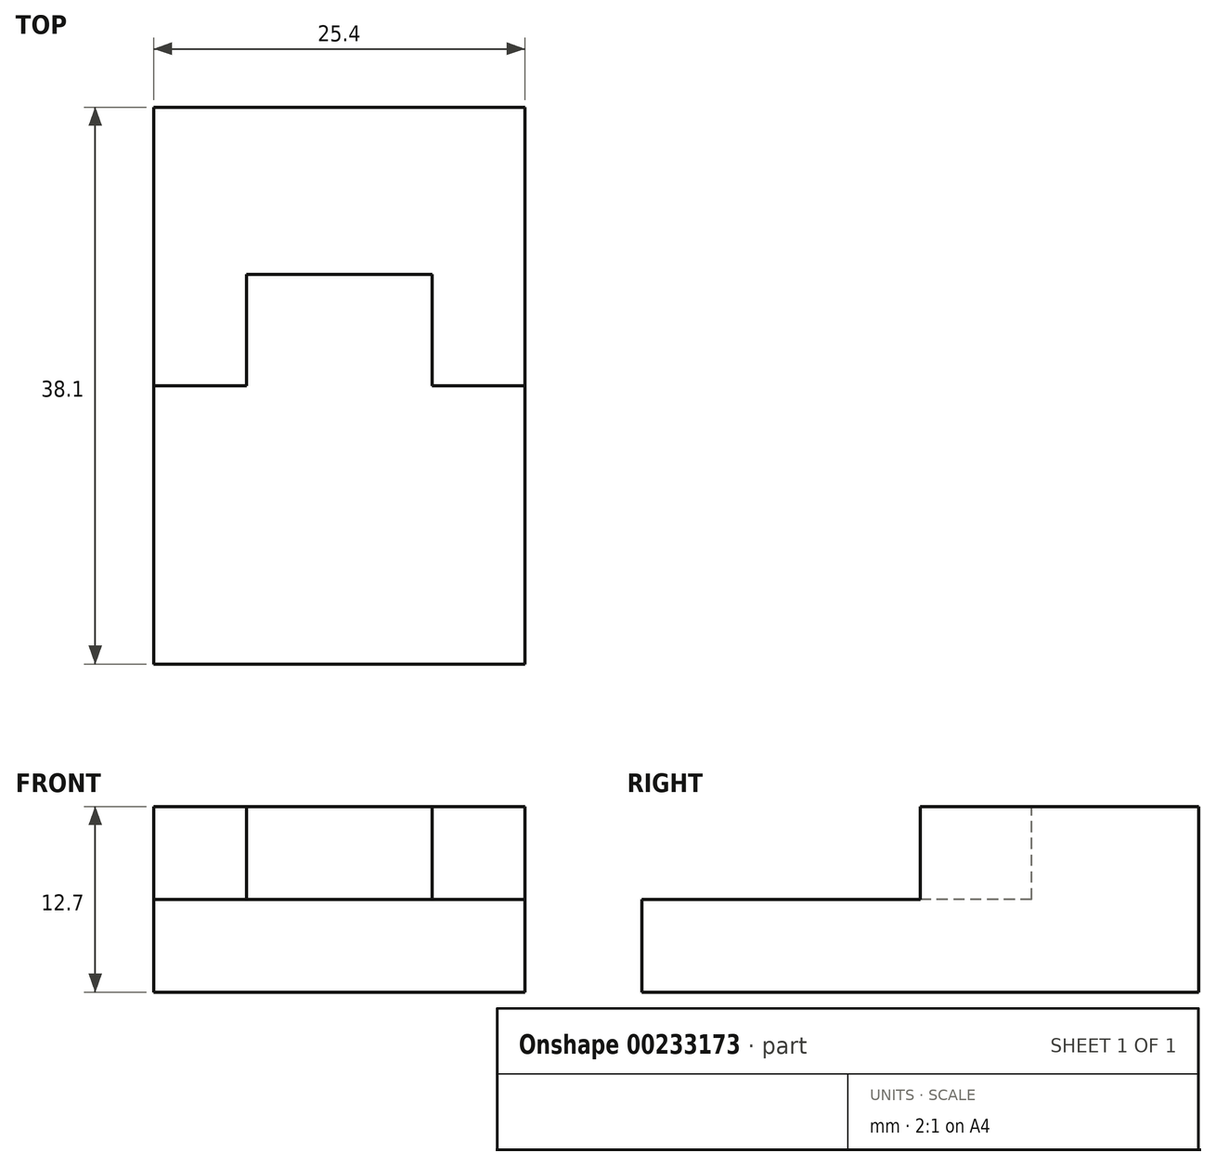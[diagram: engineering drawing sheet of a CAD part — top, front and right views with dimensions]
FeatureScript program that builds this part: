
annotation { "Feature Type Name" : "Feature", "Feature Type Description" : "" }
export const myFeature = defineFeature(function(context is Context, id is Id, definition is map)
    precondition{}
    {
        {
            var Q0;
            Q0=qCreatedBy(makeId("Top.planeOp"),FACE);
            var sketch = newSketch(context, id + "F0", { "sketchPlane" : qUnion([Q0])});
            skLineSegment(sketch, "E0.bottom", {"start": v(12.7, 19.05) * mm, "end": v(-12.7, 19.05) * mm});
            skLineSegment(sketch, "E0.top", {"start": v(12.7, -19.05) * mm, "end": v(-12.7, -19.05) * mm});
            skLineSegment(sketch, "E0.left", {"start": v(12.7, 19.05) * mm, "end": v(12.7, -19.05) * mm});
            skLineSegment(sketch, "E0.right", {"start": v(-12.7, 19.05) * mm, "end": v(-12.7, -19.05) * mm});
            skPoint(sketch, "E0.middle", {"position": v(0, 0) * mm});
            skSolve(sketch);
        }
        {
            var Q0;
            Q0 = qSketchRegion(id + "F0", true);
            extrude(context, id + "F1", {"entities" : qUnion([Q0]), "depth" : 6.35 * mm});
        }
        {
            var Q0;
            Q0=makeQuery(id+"F1.opExtrude","CAP_FACE",FACE,{"disambiguationData":[OSD([sQuery(id+"F0.wireOp",EDGE,"E0.bottom"),sQuery(id+"F0.wireOp",EDGE,"E0.top"),sQuery(id+"F0.wireOp",EDGE,"E0.left"),sQuery(id+"F0.wireOp",EDGE,"E0.right")])],"isStart":false});
            var sketch = newSketch(context, id + "F2", { "sketchPlane" : qUnion([Q0])});
            skLineSegment(sketch, "E1.bottom", {"start": v(-12.7, 0) * mm, "end": v(12.7, 0) * mm});
            skLineSegment(sketch, "E1.top", {"start": v(-12.7, 19.05) * mm, "end": v(12.7, 19.05) * mm});
            skLineSegment(sketch, "E1.left", {"start": v(-12.7, 0) * mm, "end": v(-12.7, 19.05) * mm});
            skLineSegment(sketch, "E1.right", {"start": v(12.7, 0) * mm, "end": v(12.7, 19.05) * mm});
            skSolve(sketch);
        }
        {
            var Q0;
            Q0 = qSketchRegion(id + "F2", true);
            extrude(context, id + "F3", {"entities" : qUnion([Q0]), "operationType" : NewBodyOperationType.ADD, "depth" : 6.35 * mm});
        }
        {
            var Q0;
            Q0=makeQuery(id+"F3.opExtrude","CAP_FACE",FACE,{"disambiguationData":[OSD([sQuery(id+"F2.wireOp",EDGE,"E1.bottom"),sQuery(id+"F2.wireOp",EDGE,"E1.top"),sQuery(id+"F2.wireOp",EDGE,"E1.left"),sQuery(id+"F2.wireOp",EDGE,"E1.right")])],"isStart":false});
            var sketch = newSketch(context, id + "F4", { "sketchPlane" : qUnion([Q0])});
            skLineSegment(sketch, "E2.bottom", {"start": v(6.35, 7.62) * mm, "end": v(-6.35, 7.62) * mm});
            skLineSegment(sketch, "E2.top", {"start": v(6.35, -7.62) * mm, "end": v(-6.35, -7.62) * mm});
            skLineSegment(sketch, "E2.left", {"start": v(6.35, 7.62) * mm, "end": v(6.35, -7.62) * mm});
            skLineSegment(sketch, "E2.right", {"start": v(-6.35, 7.62) * mm, "end": v(-6.35, -7.62) * mm});
            skPoint(sketch, "E2.middle", {"position": v(0, 0) * mm});
            skSolve(sketch);
        }
        {
            var Q0;
            Q0 = qSketchRegion(id + "F4", true);
            extrude(context, id + "F5", {"entities" : qUnion([Q0]), "operationType" : NewBodyOperationType.REMOVE, "endBound" : BoundingType.SYMMETRIC, "oppositeDirection" : true, "depth" : 12.7 * mm});
        }
    });
